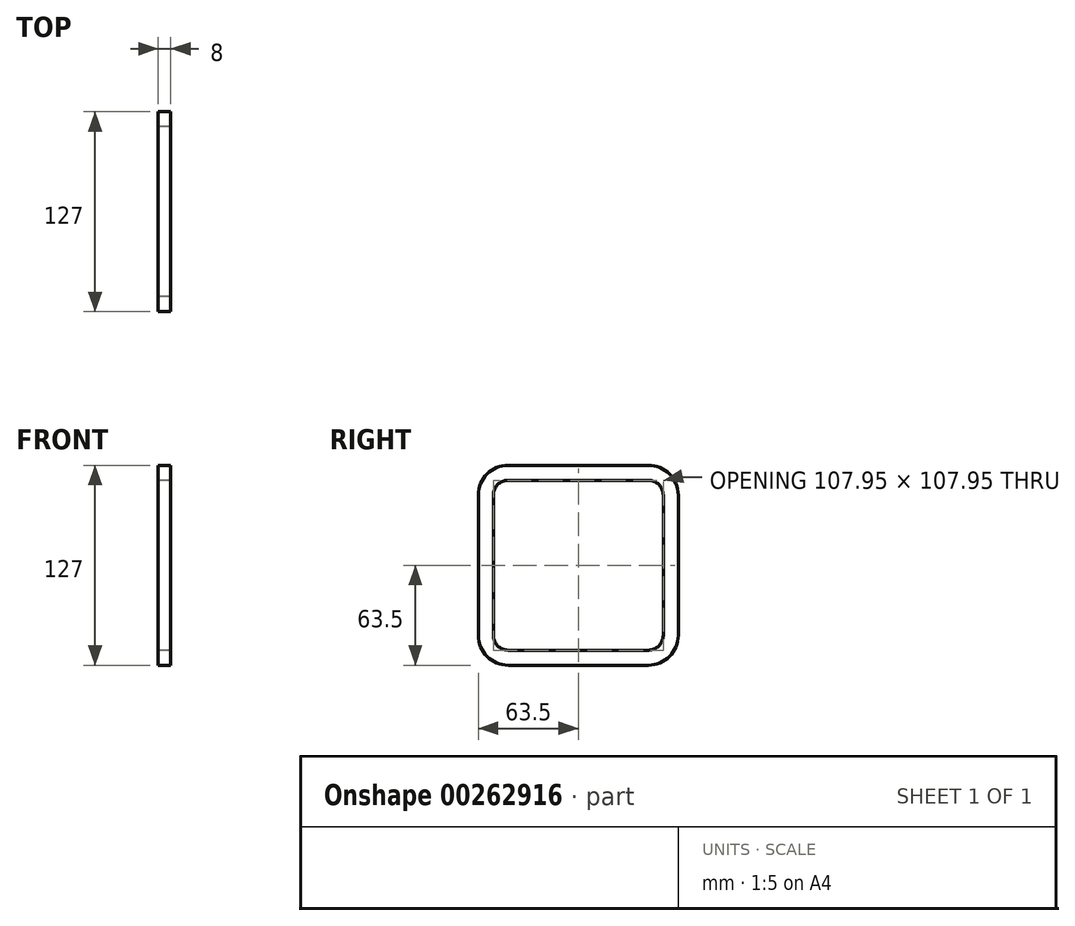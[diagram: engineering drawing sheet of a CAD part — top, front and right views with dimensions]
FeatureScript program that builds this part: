
annotation { "Feature Type Name" : "Feature", "Feature Type Description" : "" }
export const myFeature = defineFeature(function(context is Context, id is Id, definition is map)
    precondition{}
    {
        {
            assignVariable(context, id + "F0", {"name" : "Length", "anyValue" : 8});
        }
        {
            var Q0;
            Q0=qCreatedBy(makeId("Right.planeOp"),FACE);
            var sketch = newSketch(context, id + "F1", { "sketchPlane" : qUnion([Q0])});
            skLineSegment(sketch, "E0.bottom", {"start": v(-44.45, 63.5) * mm, "end": v(44.45, 63.5) * mm});
            skLineSegment(sketch, "E0.top", {"start": v(-44.45, -63.5) * mm, "end": v(44.45, -63.5) * mm});
            skLineSegment(sketch, "E0.left", {"start": v(-63.5, 44.45) * mm, "end": v(-63.5, -44.45) * mm});
            skLineSegment(sketch, "E0.right", {"start": v(63.5, 44.45) * mm, "end": v(63.5, -44.45) * mm});
            skPoint(sketch, "E0.middle", {"position": v(0, 0) * mm});
            skPoint(sketch, "E1.visualSharp", {"position": v(-63.5, 63.5) * mm});
            skArc(sketch, "E1.filletArc", {"start": v(-44.45, 63.5) * mm, "mid": v(-57.92, 57.92) * mm, "end": v(-63.5, 44.45) * mm});
            skPoint(sketch, "E2.visualSharp", {"position": v(-33.34, 46.04) * mm});
            skPoint(sketch, "E3.visualSharp", {"position": v(63.5, 63.5) * mm});
            skArc(sketch, "E3.filletArc", {"start": v(63.5, 44.45) * mm, "mid": v(57.92, 57.92) * mm, "end": v(44.45, 63.5) * mm});
            skPoint(sketch, "E4.visualSharp", {"position": v(33.34, 46.04) * mm});
            skPoint(sketch, "E5.visualSharp", {"position": v(33.34, -46.04) * mm});
            skPoint(sketch, "E6.visualSharp", {"position": v(-33.34, -46.04) * mm});
            skPoint(sketch, "E7.visualSharp", {"position": v(63.5, -63.5) * mm});
            skArc(sketch, "E7.filletArc", {"start": v(44.45, -63.5) * mm, "mid": v(57.92, -57.92) * mm, "end": v(63.5, -44.45) * mm});
            skPoint(sketch, "E8.visualSharp", {"position": v(-63.5, -63.5) * mm});
            skArc(sketch, "E8.filletArc", {"start": v(-63.5, -44.45) * mm, "mid": v(-57.92, -57.92) * mm, "end": v(-44.45, -63.5) * mm});
            skLineSegment(sketch, "E9.0", {"start": v(-44.45, 53.97) * mm, "end": v(44.45, 53.97) * mm});
            skArc(sketch, "E9.1", {"start": v(53.98, 44.45) * mm, "mid": v(51.19, 51.19) * mm, "end": v(44.45, 53.98) * mm});
            skArc(sketch, "E9.2", {"start": v(-44.45, 53.98) * mm, "mid": v(-51.19, 51.19) * mm, "end": v(-53.97, 44.45) * mm});
            skLineSegment(sketch, "E9.3", {"start": v(53.98, 44.45) * mm, "end": v(53.97, -44.45) * mm});
            skLineSegment(sketch, "E9.4", {"start": v(-53.97, 44.45) * mm, "end": v(-53.98, -44.45) * mm});
            skArc(sketch, "E9.5", {"start": v(-53.98, -44.45) * mm, "mid": v(-51.19, -51.19) * mm, "end": v(-44.45, -53.98) * mm});
            skLineSegment(sketch, "E9.6", {"start": v(-44.45, -53.97) * mm, "end": v(44.45, -53.97) * mm});
            skArc(sketch, "E9.7", {"start": v(44.45, -53.98) * mm, "mid": v(51.19, -51.19) * mm, "end": v(53.97, -44.45) * mm});
            skSolve(sketch);
        }
        {
            var Q0;
            Q0=makeQuery(id+"F1.imprint","IMPRINT",FACE,{"disambiguationData":[TD([[makeQuery(id+"F1.imprint","IMPRINT",EDGE,{"derivedFrom":sQuery(id+"F1.wireOp",EDGE,"E0.bottom")}),-1.0]])]});
            var Q1;
            Q1=sQuery(id+"F1.wireOp",EDGE,"E1.filletArc");
            var Q2;
            Q2=sQuery(id+"F1.wireOp",EDGE,"E0.left");
            var Q3;
            Q3=sQuery(id+"F1.wireOp",EDGE,"E0.bottom");
            var Q4;
            Q4=sQuery(id+"F1.wireOp",EDGE,"E3.filletArc");
            var Q5;
            Q5=sQuery(id+"F1.wireOp",EDGE,"E0.right");
            var Q6;
            Q6=sQuery(id+"F1.wireOp",EDGE,"E7.filletArc");
            var Q7;
            Q7=sQuery(id+"F1.wireOp",EDGE,"E0.top");
            var Q8;
            Q8=sQuery(id+"F1.wireOp",EDGE,"E8.filletArc");
            extrude(context, id + "F2", {"entities" : qUnion([Q0]), "surfaceEntities" : qUnion([Q1, Q2, Q3, Q4, Q5, Q6, Q7, Q8]), "endBound" : BoundingType.SYMMETRIC, "depth" : (getVariable(context, 'Length')) * mm, "hasSecondDirection" : true, "secondDirectionOppositeDirection" : true, "secondDirectionDepth" : 25.4 * mm});
        }
    });
